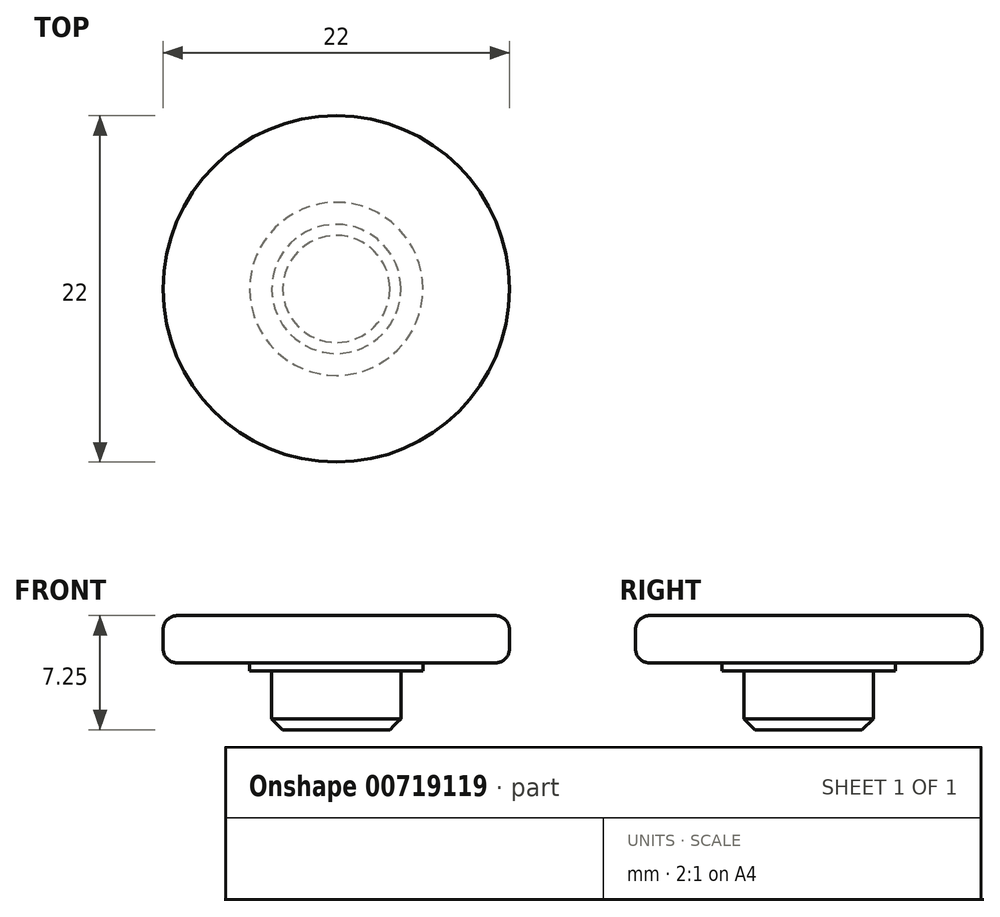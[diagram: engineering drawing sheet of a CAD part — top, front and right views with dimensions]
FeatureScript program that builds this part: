
annotation { "Feature Type Name" : "Feature", "Feature Type Description" : "" }
export const myFeature = defineFeature(function(context is Context, id is Id, definition is map)
    precondition{}
    {
        {
            var Q0;
            Q0=qCreatedBy(makeId("Top.planeOp"),FACE);
            var sketch = newSketch(context, id + "F0", { "sketchPlane" : qUnion([Q0])});
            skCircle(sketch, "E0", {"center": v(0, 0) * mm, "radius": 4.1 * mm});
            skCircle(sketch, "E1", {"center": v(0, 0) * mm, "radius": 11 * mm});
            skCircle(sketch, "E2", {"center": v(0, 0) * mm, "radius": 5.5 * mm});
            skSolve(sketch);
        }
        {
            var Q0;
            Q0=makeQuery(id+"F0.imprint","IMPRINT",FACE,{"disambiguationData":[TD([[makeQuery(id+"F0.imprint","IMPRINT",EDGE,{"derivedFrom":sQuery(id+"F0.wireOp",EDGE,"E0")}),-1.0]])]});
            var Q1;
            Q1=makeQuery(id+"F0.imprint","IMPRINT",FACE,{"disambiguationData":[TD([[makeQuery(id+"F0.imprint","IMPRINT",EDGE,{"derivedFrom":sQuery(id+"F0.wireOp",EDGE,"E0")}),1.0]])]});
            var Q2;
            Q2=makeQuery(id+"F0.imprint","IMPRINT",FACE,{"disambiguationData":[TD([[makeQuery(id+"F0.imprint","IMPRINT",EDGE,{"derivedFrom":sQuery(id+"F0.wireOp",EDGE,"E1")}),1.0]])]});
            extrude(context, id + "F1", {"entities" : qUnion([Q0, Q1, Q2]), "depth" : 3 * mm, "offsetDistance" : 25 * mm});
        }
        {
            var Q0;
            Q0=makeQuery(id+"F0.imprint","IMPRINT",FACE,{"disambiguationData":[TD([[makeQuery(id+"F0.imprint","IMPRINT",EDGE,{"derivedFrom":sQuery(id+"F0.wireOp",EDGE,"E0")}),1.0]])]});
            extrude(context, id + "F2", {"entities" : qUnion([Q0]), "operationType" : NewBodyOperationType.ADD, "oppositeDirection" : true, "depth" : 4.25 * mm, "offsetDistance" : 25 * mm});
        }
        {
            var Q0;
            Q0=makeQuery(id+"F2.opExtrude","CAP_FACE",FACE,{"disambiguationData":[OSD([sQuery(id+"F0.wireOp",EDGE,"E0")])],"isStart":false});
            chamfer(context, id + "F3", {"entities" : qUnion([Q0]), "width" : 0.7 * mm});
        }
        {
            var Q0;
            Q0=makeQuery(id+"F1.opExtrude","SWEPT_FACE",FACE,{"disambiguationData":[OSD([sQuery(id+"F0.wireOp",EDGE,"E1")])]});
            fillet(context, id + "F4", {"entities" : qUnion([Q0]), "radius" : 0.9 * mm, "allowEdgeOverflow" : false});
        }
        {
            var Q0;
            Q0=makeQuery(id+"F0.imprint","IMPRINT",FACE,{"disambiguationData":[TD([[makeQuery(id+"F0.imprint","IMPRINT",EDGE,{"derivedFrom":sQuery(id+"F0.wireOp",EDGE,"E0")}),-1.0]])]});
            extrude(context, id + "F5", {"entities" : qUnion([Q0]), "operationType" : NewBodyOperationType.ADD, "oppositeDirection" : true, "depth" : .5 * mm, "offsetDistance" : 25 * mm});
        }
    });
